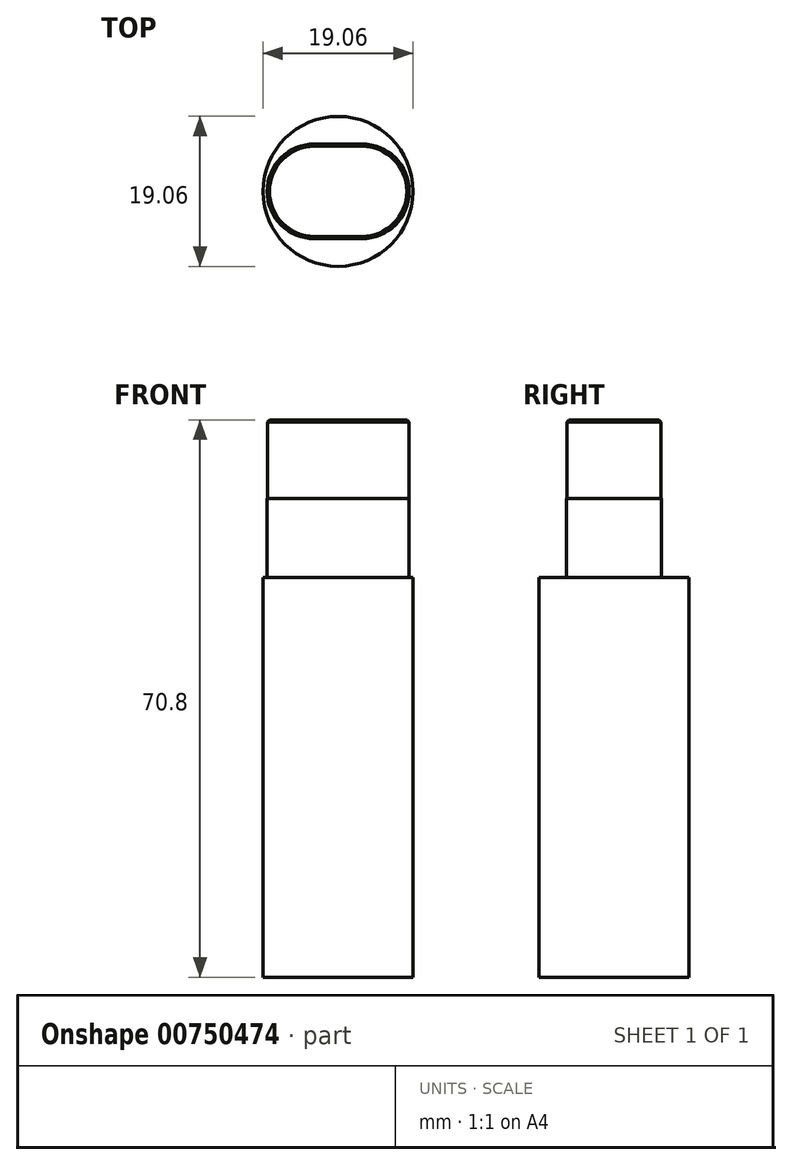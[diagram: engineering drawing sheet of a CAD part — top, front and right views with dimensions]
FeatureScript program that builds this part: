
annotation { "Feature Type Name" : "Feature", "Feature Type Description" : "" }
export const myFeature = defineFeature(function(context is Context, id is Id, definition is map)
    precondition{}
    {
        {
            var Q0;
            Q0=qCreatedBy(makeId("Top.planeOp"),FACE);
            var sketch = newSketch(context, id + "F0", { "sketchPlane" : qUnion([Q0])});
            skCircle(sketch, "E0", {"center": v(0, 0) * mm, "radius": 9.52 * mm});
            skSolve(sketch);
        }
        {
            var Q0;
            Q0=qSketchRegion(id+"F0",true);
            extrude(context, id + "F1", {"entities" : qUnion([Q0]), "depth" : 50.8 * mm, "offsetDistance" : 25.4 * mm});
        }
        {
            var Q0;
            Q0=makeQuery(id+"F1.opExtrude","CAP_FACE",FACE,{"disambiguationData":[OSD([sQuery(id+"F0.wireOp",EDGE,"E0")])],"isStart":false});
            var sketch = newSketch(context, id + "F2", { "sketchPlane" : qUnion([Q0])});
            skLineSegment(sketch, "E1", {"start": v(0, 0) * mm, "end": v(9.03, 0) * mm});
            skLineSegment(sketch, "E2", {"start": v(0, 0) * mm, "end": v(-9.03, 0) * mm});
            skLineSegment(sketch, "E3", {"start": v(0, 0) * mm, "end": v(0, 6.03) * mm});
            skLineSegment(sketch, "E4", {"start": v(0, 0) * mm, "end": v(0, -6.03) * mm});
            skLineSegment(sketch, "E5", {"start": v(9.03, 0) * mm, "end": v(3, 0) * mm});
            skLineSegment(sketch, "E6", {"start": v(-9.03, 0) * mm, "end": v(-3, 0) * mm});
            skArc(sketch, "E7", {"start": v(3, -6.03) * mm, "mid": v(9.03, 0) * mm, "end": v(3, 6.03) * mm});
            skArc(sketch, "E8", {"start": v(-3, -6.03) * mm, "mid": v(-9.03, 0) * mm, "end": v(-3, 6.03) * mm});
            skLineSegment(sketch, "E9", {"start": v(-3, 6.03) * mm, "end": v(3, 6.03) * mm});
            skLineSegment(sketch, "E10", {"start": v(3, -6.03) * mm, "end": v(-3, -6.03) * mm});
            skSolve(sketch);
        }
        {
            var Q0;
            Q0=qSketchRegion(id+"F2",true);
            extrude(context, id + "F3", {"entities" : qUnion([Q0]), "operationType" : NewBodyOperationType.ADD, "depth" : 10 * mm, "offsetDistance" : 25 * mm});
        }
        {
            var Q0;
            Q0=makeQuery(id+"F3.opExtrude","CAP_FACE",FACE,{"disambiguationData":[OSD([sQuery(id+"F2.wireOp",EDGE,"E7"),sQuery(id+"F2.wireOp",EDGE,"E8"),sQuery(id+"F2.wireOp",EDGE,"E9"),sQuery(id+"F2.wireOp",EDGE,"E10")])],"isStart":false});
            var sketch = newSketch(context, id + "F4", { "sketchPlane" : qUnion([Q0])});
            skLineSegment(sketch, "E11", {"start": v(0, 0) * mm, "end": v(8.97, 0) * mm});
            skLineSegment(sketch, "E12", {"start": v(8.97, 0) * mm, "end": v(3, 0) * mm});
            skLineSegment(sketch, "E13", {"start": v(0, 0) * mm, "end": v(-8.97, 0) * mm});
            skLineSegment(sketch, "E14", {"start": v(-8.97, 0) * mm, "end": v(-3, 0) * mm});
            skLineSegment(sketch, "E15", {"start": v(0, 0) * mm, "end": v(0, 5.97) * mm});
            skLineSegment(sketch, "E16", {"start": v(0, 0) * mm, "end": v(0, -5.97) * mm});
            skArc(sketch, "E17", {"start": v(3, -5.97) * mm, "mid": v(8.97, 0) * mm, "end": v(3, 5.97) * mm});
            skArc(sketch, "E18", {"start": v(-3, 5.97) * mm, "mid": v(-8.97, 0) * mm, "end": v(-3, -5.97) * mm});
            skLineSegment(sketch, "E19", {"start": v(-3, -5.97) * mm, "end": v(3, -5.97) * mm});
            skLineSegment(sketch, "E20", {"start": v(3, 5.97) * mm, "end": v(-3, 5.97) * mm});
            skSolve(sketch);
        }
        {
            var Q0;
            Q0=qSketchRegion(id+"F4",true);
            extrude(context, id + "F5", {"entities" : qUnion([Q0]), "operationType" : NewBodyOperationType.ADD, "depth" : 10 * mm, "offsetDistance" : 25 * mm});
        }
        {
            var Q0;
            Q0=makeQuery(id+"F5.opExtrude","CAP_EDGE",EDGE,{"disambiguationData":[OSD([sQuery(id+"F4.wireOp",EDGE,"E19")])],"isStart":false});
            chamfer(context, id + "F6", {"entities" : qUnion([Q0]), "width" : .25 * mm, "tangentPropagation" : true});
        }
    });
